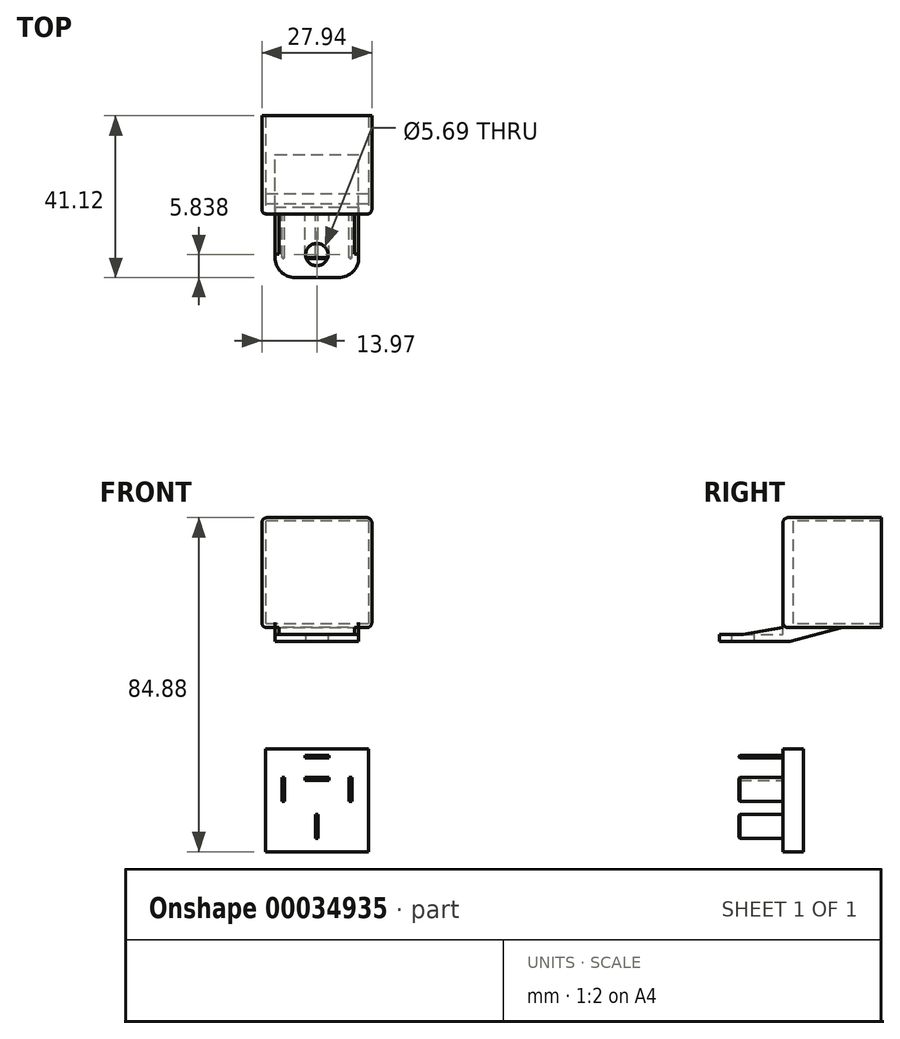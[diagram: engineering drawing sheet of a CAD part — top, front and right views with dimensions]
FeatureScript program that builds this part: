
annotation { "Feature Type Name" : "Feature", "Feature Type Description" : "" }
export const myFeature = defineFeature(function(context is Context, id is Id, definition is map)
    precondition{}
    {
        {
            var Q0;
            Q0=qCreatedBy(makeId("Front.planeOp"),FACE);
            var sketch = newSketch(context, id + "F0", { "sketchPlane" : qUnion([Q0])});
            skLineSegment(sketch, "E0.rect.bottom", {"start": v(13.08, 13.08) * mm, "end": v(-13.08, 13.08) * mm});
            skLineSegment(sketch, "E0.rect.top", {"start": v(13.08, -13.08) * mm, "end": v(-13.08, -13.08) * mm});
            skLineSegment(sketch, "E0.rect.left", {"start": v(13.08, 13.08) * mm, "end": v(13.08, -13.08) * mm});
            skLineSegment(sketch, "E0.rect.right", {"start": v(-13.08, 13.08) * mm, "end": v(-13.08, -13.08) * mm});
            skPoint(sketch, "E0.rect.middle", {"position": v(0, 0) * mm});
            skLineSegment(sketch, "E1.bottom", {"start": v(-0.33, -9.65) * mm, "end": v(0.33, -9.65) * mm});
            skLineSegment(sketch, "E1.top", {"start": v(-0.33, -3.56) * mm, "end": v(0.33, -3.56) * mm});
            skLineSegment(sketch, "E1.left", {"start": v(-0.33, -9.65) * mm, "end": v(-0.33, -3.56) * mm});
            skLineSegment(sketch, "E1.right", {"start": v(0.33, -9.65) * mm, "end": v(0.33, -3.56) * mm});
            skLineSegment(sketch, "E2.left", {"start": v(-8.9, -0.33) * mm, "end": v(-8.9, 5.77) * mm});
            skLineSegment(sketch, "E2.top", {"start": v(-8.9, 5.77) * mm, "end": v(-8.23, 5.77) * mm});
            skLineSegment(sketch, "E2.right", {"start": v(-8.23, -0.33) * mm, "end": v(-8.23, 5.77) * mm});
            skLineSegment(sketch, "E2.bottom", {"start": v(-8.89, -0.33) * mm, "end": v(-8.23, -0.33) * mm});
            skLineSegment(sketch, "E3.left", {"start": v(8.23, -0.33) * mm, "end": v(8.23, 5.77) * mm});
            skLineSegment(sketch, "E3.top", {"start": v(8.23, 5.77) * mm, "end": v(8.9, 5.77) * mm});
            skLineSegment(sketch, "E3.right", {"start": v(8.9, -0.33) * mm, "end": v(8.89, 5.77) * mm});
            skLineSegment(sketch, "E3.bottom", {"start": v(8.23, -0.33) * mm, "end": v(8.9, -0.33) * mm});
            skPoint(sketch, "E4", {"position": v(0, -3.56) * mm});
            skLineSegment(sketch, "E5", {"start": v(-17.88, 5.77) * mm, "end": v(17.67, 5.77) * mm, "construction": true});
            skLineSegment(sketch, "E6", {"start": v(8.9, 14.98) * mm, "end": v(8.9, -16.04) * mm, "construction": true});
            skLineSegment(sketch, "E7.MirrorCS", {"start": v(-8.9, 14.98) * mm, "end": v(-8.9, -16.04) * mm, "construction": true});
            skPoint(sketch, "E8", {"position": v(8.9, 5.77) * mm});
            skPoint(sketch, "E9", {"position": v(-8.9, 5.77) * mm});
            skLineSegment(sketch, "E10.bottom", {"start": v(-3.05, 5.77) * mm, "end": v(3.05, 5.77) * mm});
            skLineSegment(sketch, "E10.top", {"start": v(-3.05, 5.1) * mm, "end": v(3.05, 5.1) * mm});
            skLineSegment(sketch, "E10.left", {"start": v(-3.05, 5.77) * mm, "end": v(-3.05, 5.1) * mm});
            skLineSegment(sketch, "E10.right", {"start": v(3.05, 5.77) * mm, "end": v(3.05, 5.1) * mm});
            skLineSegment(sketch, "E11.bottom", {"start": v(-3.05, 11.4) * mm, "end": v(3.05, 11.4) * mm});
            skLineSegment(sketch, "E11.top", {"start": v(-3.05, 10.74) * mm, "end": v(3.05, 10.74) * mm});
            skLineSegment(sketch, "E11.left", {"start": v(-3.05, 11.4) * mm, "end": v(-3.05, 10.74) * mm});
            skLineSegment(sketch, "E11.right", {"start": v(3.05, 11.4) * mm, "end": v(3.05, 10.74) * mm});
            skLineSegment(sketch, "E12", {"start": v(-16.62, 11.4) * mm, "end": v(16.69, 11.4) * mm, "construction": true});
            skLineSegment(sketch, "E13", {"start": v(-18.26, 3.56) * mm, "end": v(16.3, 3.56) * mm, "construction": true});
            skPoint(sketch, "E14", {"position": v(0, 5.77) * mm});
            skPoint(sketch, "E15", {"position": v(0, 11.4) * mm});
            skPoint(sketch, "E15.positionSnap0", {"position": v(0, 13.08) * mm});
            skSolve(sketch);
        }
        {
            var Q0;
            Q0 = qSketchRegion(id + "F0", true);
            var Q1;
            Q1=makeQuery(id+"F0.imprint","IMPRINT",FACE,{"disambiguationData":[TD([[makeQuery(id+"F0.imprint","IMPRINT",EDGE,{"derivedFrom":sQuery(id+"F0.wireOp",EDGE,"E11.bottom")}),-1.0]])]});
            var Q2;
            Q2=makeQuery(id+"F0.imprint","IMPRINT",FACE,{"disambiguationData":[TD([[makeQuery(id+"F0.imprint","IMPRINT",EDGE,{"derivedFrom":sQuery(id+"F0.wireOp",EDGE,"E10.bottom")}),-1.0]])]});
            var Q3;
            Q3=makeQuery(id+"F0.imprint","IMPRINT",FACE,{"disambiguationData":[TD([[makeQuery(id+"F0.imprint","IMPRINT",EDGE,{"derivedFrom":sQuery(id+"F0.wireOp",EDGE,"E2.left")}),-1.0]])]});
            var Q4;
            Q4=makeQuery(id+"F0.imprint","IMPRINT",FACE,{"disambiguationData":[TD([[makeQuery(id+"F0.imprint","IMPRINT",EDGE,{"derivedFrom":sQuery(id+"F0.wireOp",EDGE,"E3.left")}),-1.0]])]});
            var Q5;
            Q5=makeQuery(id+"F0.imprint","IMPRINT",FACE,{"disambiguationData":[TD([[makeQuery(id+"F0.imprint","IMPRINT",EDGE,{"derivedFrom":sQuery(id+"F0.wireOp",EDGE,"E1.bottom")}),1.0]])]});
            extrude(context, id + "F1", {"entities" : qUnion([Q0, Q1, Q2, Q3, Q4, Q5]), "oppositeDirection" : true, "depth" : 5.13 * mm});
        }
        {
            var Q0;
            Q0=makeQuery(id+"F0.imprint","IMPRINT",FACE,{"disambiguationData":[TD([[makeQuery(id+"F0.imprint","IMPRINT",EDGE,{"derivedFrom":sQuery(id+"F0.wireOp",EDGE,"E11.bottom")}),-1.0]])]});
            var Q1;
            Q1=makeQuery(id+"F0.imprint","IMPRINT",FACE,{"disambiguationData":[TD([[makeQuery(id+"F0.imprint","IMPRINT",EDGE,{"derivedFrom":sQuery(id+"F0.wireOp",EDGE,"E10.bottom")}),-1.0]])]});
            var Q2;
            Q2=makeQuery(id+"F0.imprint","IMPRINT",FACE,{"disambiguationData":[TD([[makeQuery(id+"F0.imprint","IMPRINT",EDGE,{"derivedFrom":sQuery(id+"F0.wireOp",EDGE,"E2.left")}),-1.0]])]});
            var Q3;
            Q3=makeQuery(id+"F0.imprint","IMPRINT",FACE,{"disambiguationData":[TD([[makeQuery(id+"F0.imprint","IMPRINT",EDGE,{"derivedFrom":sQuery(id+"F0.wireOp",EDGE,"E3.left")}),-1.0]])]});
            var Q4;
            Q4=makeQuery(id+"F0.imprint","IMPRINT",FACE,{"disambiguationData":[TD([[makeQuery(id+"F0.imprint","IMPRINT",EDGE,{"derivedFrom":sQuery(id+"F0.wireOp",EDGE,"E1.bottom")}),1.0]])]});
            extrude(context, id + "F2", {"entities" : qUnion([Q0, Q1, Q2, Q3, Q4]), "operationType" : NewBodyOperationType.ADD, "depth" : 11.25 * mm});
        }
        {
            var Q0;
            Q0=makeQuery(id+"F2.opExtrude","CAP_EDGE",EDGE,{"disambiguationData":[OSD([sQuery(id+"F0.wireOp",EDGE,"E10.bottom")])],"isStart":false});
            var Q1;
            Q1=makeQuery(id+"F2.opExtrude","CAP_EDGE",EDGE,{"disambiguationData":[OSD([sQuery(id+"F0.wireOp",EDGE,"E10.top")])],"isStart":false});
            var Q2;
            Q2=makeQuery(id+"F2.opExtrude","CAP_EDGE",EDGE,{"disambiguationData":[OSD([sQuery(id+"F0.wireOp",EDGE,"E10.left")])],"isStart":false});
            var Q3;
            Q3=makeQuery(id+"F2.opExtrude","CAP_EDGE",EDGE,{"disambiguationData":[OSD([sQuery(id+"F0.wireOp",EDGE,"E10.right")])],"isStart":false});
            var Q4;
            Q4=makeQuery(id+"F2.opExtrude","CAP_EDGE",EDGE,{"disambiguationData":[OSD([sQuery(id+"F0.wireOp",EDGE,"E11.bottom")])],"isStart":false});
            var Q5;
            Q5=makeQuery(id+"F2.opExtrude","CAP_EDGE",EDGE,{"disambiguationData":[OSD([sQuery(id+"F0.wireOp",EDGE,"E11.top")])],"isStart":false});
            var Q6;
            Q6=makeQuery(id+"F2.opExtrude","CAP_EDGE",EDGE,{"disambiguationData":[OSD([sQuery(id+"F0.wireOp",EDGE,"E11.left")])],"isStart":false});
            var Q7;
            Q7=makeQuery(id+"F2.opExtrude","CAP_EDGE",EDGE,{"disambiguationData":[OSD([sQuery(id+"F0.wireOp",EDGE,"E11.right")])],"isStart":false});
            var Q8;
            Q8=makeQuery(id+"F2.opExtrude","CAP_EDGE",EDGE,{"disambiguationData":[OSD([sQuery(id+"F0.wireOp",EDGE,"E3.top")])],"isStart":false});
            var Q9;
            Q9=makeQuery(id+"F2.opExtrude","CAP_EDGE",EDGE,{"disambiguationData":[OSD([sQuery(id+"F0.wireOp",EDGE,"E3.right")])],"isStart":false});
            var Q10;
            Q10=makeQuery(id+"F2.opExtrude","CAP_EDGE",EDGE,{"disambiguationData":[OSD([sQuery(id+"F0.wireOp",EDGE,"E3.left")])],"isStart":false});
            var Q11;
            Q11=makeQuery(id+"F2.opExtrude","CAP_EDGE",EDGE,{"disambiguationData":[OSD([sQuery(id+"F0.wireOp",EDGE,"E3.bottom")])],"isStart":false});
            var Q12;
            Q12=makeQuery(id+"F2.opExtrude","CAP_EDGE",EDGE,{"disambiguationData":[OSD([sQuery(id+"F0.wireOp",EDGE,"E2.top")])],"isStart":false});
            var Q13;
            Q13=makeQuery(id+"F2.opExtrude","CAP_EDGE",EDGE,{"disambiguationData":[OSD([sQuery(id+"F0.wireOp",EDGE,"E2.right")])],"isStart":false});
            var Q14;
            Q14=makeQuery(id+"F2.opExtrude","CAP_EDGE",EDGE,{"disambiguationData":[OSD([sQuery(id+"F0.wireOp",EDGE,"E2.left")])],"isStart":false});
            var Q15;
            Q15=makeQuery(id+"F2.opExtrude","CAP_EDGE",EDGE,{"disambiguationData":[OSD([sQuery(id+"F0.wireOp",EDGE,"E2.bottom")])],"isStart":false});
            var Q16;
            Q16=makeQuery(id+"F2.opExtrude","CAP_EDGE",EDGE,{"disambiguationData":[OSD([sQuery(id+"F0.wireOp",EDGE,"E1.top")])],"isStart":false});
            var Q17;
            Q17=makeQuery(id+"F2.opExtrude","CAP_EDGE",EDGE,{"disambiguationData":[OSD([sQuery(id+"F0.wireOp",EDGE,"E1.right")])],"isStart":false});
            var Q18;
            Q18=makeQuery(id+"F2.opExtrude","CAP_EDGE",EDGE,{"disambiguationData":[OSD([sQuery(id+"F0.wireOp",EDGE,"E1.left")])],"isStart":false});
            var Q19;
            Q19=makeQuery(id+"F2.opExtrude","CAP_EDGE",EDGE,{"disambiguationData":[OSD([sQuery(id+"F0.wireOp",EDGE,"E1.bottom")])],"isStart":false});
            chamfer(context, id + "F3", {"entities" : qUnion([Q0, Q1, Q2, Q3, Q4, Q5, Q6, Q7, Q8, Q9, Q10, Q11, Q12, Q13, Q14, Q15, Q16, Q17, Q18, Q19]), "width" : 0.25 * mm, "tangentPropagation" : true});
        }
        {
            var Q0;
            Q0=qCreatedBy(makeId("Front.planeOp"),FACE);
            var sketch = newSketch(context, id + "F4", { "sketchPlane" : qUnion([Q0])});
            skLineSegment(sketch, "E16", {"start": v(-31.04, 57.83) * mm, "end": v(32.27, 57.83) * mm, "construction": true});
            skLineSegment(sketch, "E17", {"start": v(0, 81.04) * mm, "end": v(0, 29.52) * mm, "construction": true});
            skLineSegment(sketch, "E18.rect.bottom", {"start": v(13.08, 70.9) * mm, "end": v(-13.08, 70.9) * mm});
            skLineSegment(sketch, "E18.rect.top", {"start": v(13.08, 44.75) * mm, "end": v(-13.08, 44.75) * mm});
            skLineSegment(sketch, "E18.rect.left", {"start": v(13.08, 70.9) * mm, "end": v(13.08, 44.75) * mm});
            skLineSegment(sketch, "E18.rect.right", {"start": v(-13.08, 70.9) * mm, "end": v(-13.08, 44.75) * mm});
            skPoint(sketch, "E18.rect.middle", {"position": v(0, 57.83) * mm});
            skLineSegment(sketch, "E19.rect.bottom", {"start": v(13.97, 71.8) * mm, "end": v(-13.97, 71.8) * mm});
            skLineSegment(sketch, "E19.rect.top", {"start": v(13.97, 43.86) * mm, "end": v(-13.97, 43.86) * mm});
            skLineSegment(sketch, "E19.rect.left", {"start": v(13.97, 71.8) * mm, "end": v(13.97, 43.86) * mm});
            skLineSegment(sketch, "E19.rect.right", {"start": v(-13.97, 71.8) * mm, "end": v(-13.97, 43.86) * mm});
            skSolve(sketch);
        }
        {
            var Q0;
            Q0 = qSketchRegion(id + "F4", true);
            var Q1;
            Q1=makeQuery(id+"F4.imprint","IMPRINT",FACE,{"disambiguationData":[TD([[makeQuery(id+"F4.imprint","IMPRINT",EDGE,{"derivedFrom":sQuery(id+"F4.wireOp",EDGE,"E18.rect.bottom")}),1.0]])]});
            extrude(context, id + "F5", {"entities" : qUnion([Q0, Q1]), "oppositeDirection" : true, "depth" : 25.02 * mm});
        }
        {
            var Q0;
            Q0=makeQuery(id+"F4.imprint","IMPRINT",FACE,{"disambiguationData":[TD([[makeQuery(id+"F4.imprint","IMPRINT",EDGE,{"derivedFrom":sQuery(id+"F4.wireOp",EDGE,"E18.rect.bottom")}),1.0]])]});
            extrude(context, id + "F6", {"entities" : qUnion([Q0]), "operationType" : NewBodyOperationType.REMOVE, "oppositeDirection" : true, "depth" : 27.94 * mm, "hasSecondDirection" : true, "secondDirectionOppositeDirection" : true, "secondDirectionDepth" : 2.54 * mm});
        }
        {
            var Q0;
            Q0=qCreatedBy(makeId("Right.planeOp"),FACE);
            var sketch = newSketch(context, id + "F7", { "sketchPlane" : qUnion([Q0])});
            skLineSegment(sketch, "E20", {"start": v(1.71, 40.4) * mm, "end": v(-16.1, 40.4) * mm});
            skLineSegment(sketch, "E21", {"start": v(-10.16, 42.18) * mm, "end": v(-16.1, 42.18) * mm});
            skPoint(sketch, "E22.orphan", {"position": v(44.7, 40.4) * mm});
            skLineSegment(sketch, "E23", {"start": v(0, 43.88) * mm, "end": v(33.36, 43.88) * mm, "construction": true});
            skLineSegment(sketch, "E24", {"start": v(1.71, 40.4) * mm, "end": v(15.24, 43.88) * mm});
            skLineSegment(sketch, "E25", {"start": v(0, 43.88) * mm, "end": v(-10.16, 42.18) * mm});
            skLineSegment(sketch, "E26", {"start": v(-16.1, 42.18) * mm, "end": v(-16.1, 40.4) * mm});
            skPoint(sketch, "E27.orphan", {"position": v(-51.33, 40.4) * mm});
            skLineSegment(sketch, "E28", {"start": v(-10.16, 42.18) * mm, "end": v(0, 42.18) * mm});
            skLineSegment(sketch, "E29", {"start": v(0, 42.18) * mm, "end": v(0, 43.88) * mm});
            skLineSegment(sketch, "E30", {"start": v(15.24, 43.88) * mm, "end": v(0, 43.88) * mm});
            skSolve(sketch);
        }
        {
            var Q0;
            Q0 = qSketchRegion(id + "F7", true);
            extrude(context, id + "F8", {"entities" : qUnion([Q0]), "operationType" : NewBodyOperationType.ADD, "endBound" : BoundingType.SYMMETRIC, "depth" : 21.26 * mm});
        }
        {
            var Q0;
            Q0=makeQuery(id+"F7.imprint","IMPRINT",FACE,{"disambiguationData":[TD([[makeQuery(id+"F7.imprint","IMPRINT",EDGE,{"derivedFrom":sQuery(id+"F7.wireOp",EDGE,"E25")}),1.0]])]});
            extrude(context, id + "F9", {"entities" : qUnion([Q0]), "operationType" : NewBodyOperationType.REMOVE, "endBound" : BoundingType.SYMMETRIC, "oppositeDirection" : true, "depth" : 19.23 * mm});
        }
        {
            var Q0;
            Q0=makeQuery(id+"F8.opExtrude","SWEPT_FACE",FACE,{"disambiguationData":[OSD([sQuery(id+"F7.wireOp",EDGE,"E20")])]});
            var sketch = newSketch(context, id + "F10", { "sketchPlane" : qUnion([Q0])});
            skLineSegment(sketch, "E31", {"start": v(-17.1, 10.26) * mm, "end": v(17.28, 10.26) * mm, "construction": true});
            skCircle(sketch, "E32", {"center": v(0, 10.26) * mm, "radius": 2.84 * mm});
            skPoint(sketch, "E32.centerSnap0", {"position": v(0, 16.1) * mm});
            skSolve(sketch);
        }
        {
            var Q0;
            Q0 = qSketchRegion(id + "F10", true);
            extrude(context, id + "F11", {"entities" : qUnion([Q0]), "operationType" : NewBodyOperationType.REMOVE, "endBound" : BoundingType.UP_TO_NEXT, "oppositeDirection" : true, "depth" : 25.4 * mm});
        }
        {
            var Q0;
            Q0=makeQuery(id+"F8.opExtrude","CAP_EDGE",EDGE,{"disambiguationData":[OSD([sQuery(id+"F7.wireOp",EDGE,"E26")])],"isStart":true});
            var Q1;
            Q1=makeQuery(id+"F8.opExtrude","CAP_EDGE",EDGE,{"disambiguationData":[OSD([sQuery(id+"F7.wireOp",EDGE,"E26")])],"isStart":false});
            fillet(context, id + "F12", {"entities" : qUnion([Q0, Q1]), "radius" : 5.08 * mm, "tangentPropagation" : true, "allowEdgeOverflow" : false});
        }
        {
            var Q0;
            Q0=makeQuery(id+"F5.opExtrude","CAP_EDGE",EDGE,{"disambiguationData":[OSD([sQuery(id+"F4.wireOp",EDGE,"E19.rect.left")])],"isStart":true});
            var Q1;
            Q1=makeQuery(id+"F5.opExtrude","SWEPT_EDGE",EDGE,{"disambiguationData":[OSD([sQuery(id+"F4.wireOp",EDGE,"E19.rect.bottom"),sQuery(id+"F4.wireOp",EDGE,"E19.rect.left")])]});
            var Q2;
            Q2=makeQuery(id+"F5.opExtrude","CAP_EDGE",EDGE,{"disambiguationData":[OSD([sQuery(id+"F4.wireOp",EDGE,"E19.rect.bottom")])],"isStart":true});
            var Q3;
            Q3=makeQuery(id+"F5.opExtrude","SWEPT_EDGE",EDGE,{"disambiguationData":[OSD([sQuery(id+"F4.wireOp",EDGE,"E19.rect.bottom"),sQuery(id+"F4.wireOp",EDGE,"E19.rect.right")])]});
            var Q4;
            Q4=makeQuery(id+"F5.opExtrude","SWEPT_EDGE",EDGE,{"disambiguationData":[OSD([sQuery(id+"F4.wireOp",EDGE,"E19.rect.top"),sQuery(id+"F4.wireOp",EDGE,"E19.rect.right")])]});
            var Q5;
            Q5=makeQuery(id+"F5.opExtrude","CAP_EDGE",EDGE,{"disambiguationData":[OSD([sQuery(id+"F4.wireOp",EDGE,"E19.rect.right")])],"isStart":true});
            var Q6;
            {var subQ0=sQuery(id+"F4.wireOp",EDGE,"E19.rect.top");var subQ1=sQuery(id+"F4.wireOp",EDGE,"E19.rect.right");Q6=makeQuery(id+"F8.boolean.opBoolean","SPLIT",EDGE,{"disambiguationData":[TD([makeQuery(id+"F5.opExtrude","SWEPT_FACE",FACE,{"disambiguationData":[OSD([subQ1])]})])],"derivedFrom":makeQuery(id+"F5.opExtrude","CAP_EDGE",EDGE,{"disambiguationData":[OSD([subQ0])],"isStart":true})});}
            var Q7;
            {var subQ0=sQuery(id+"F4.wireOp",EDGE,"E19.rect.top");var subQ1=sQuery(id+"F4.wireOp",EDGE,"E19.rect.left");Q7=makeQuery(id+"F8.boolean.opBoolean","SPLIT",EDGE,{"disambiguationData":[TD([makeQuery(id+"F5.opExtrude","SWEPT_FACE",FACE,{"disambiguationData":[OSD([subQ1])]})])],"derivedFrom":makeQuery(id+"F5.opExtrude","CAP_EDGE",EDGE,{"disambiguationData":[OSD([subQ0])],"isStart":true})});}
            var Q8;
            Q8=makeQuery(id+"F5.opExtrude","SWEPT_EDGE",EDGE,{"disambiguationData":[OSD([sQuery(id+"F4.wireOp",EDGE,"E19.rect.top"),sQuery(id+"F4.wireOp",EDGE,"E19.rect.left")])]});
            fillet(context, id + "F13", {"entities" : qUnion([Q0, Q1, Q2, Q3, Q4, Q5, Q6, Q7, Q8]), "radius" : 1.27 * mm, "tangentPropagation" : true, "allowEdgeOverflow" : false});
        }
    });
